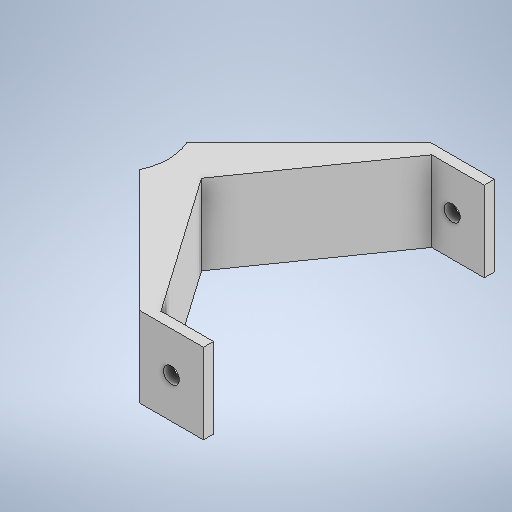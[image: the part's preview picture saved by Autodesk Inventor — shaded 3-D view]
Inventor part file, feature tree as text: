
AUTODESK INVENTOR PART (.ipt)
format: ipt  version: 2025.1 (Build 291241000, 241)  size: 253,952 bytes
history: native  units: in
note: dims shown in document units (in); Inventor stores cm internally (conversion verified against a paired STEP export)
features: extrude x2, sketch x2
ambient origin geometry x8: Origin, YZ Plane, XZ Plane, XY Plane, X Axis, Y Axis, Z Axis, Center Point
bodies: Solid1 (feature_tree)
feature tree (4):
  extrude  "Extrusion1"  TaperAngle=0.0deg  [1 undecoded]
  extrude  "Extrusion2"  Depth=3.625in
  sketch  "Sketch1"  dims[d1=0.8in d6=0.0in]
  sketch  "Sketch2"  dims[d17=1.0in d18=0.0in d19=0.4in d20=0.2in d21=5.625in d22=0.0in d26=1.0in d27=45.0deg d29=45.0deg d31=0.3779in d34=3.625in d23=0.0in d24=0.0in d25=0.0in]
note: 1 required parameter value undecoded (feature->parameter linkage not recoverable at this tier; creation-order binding heuristic only, values carry confidence <= 0.55)
